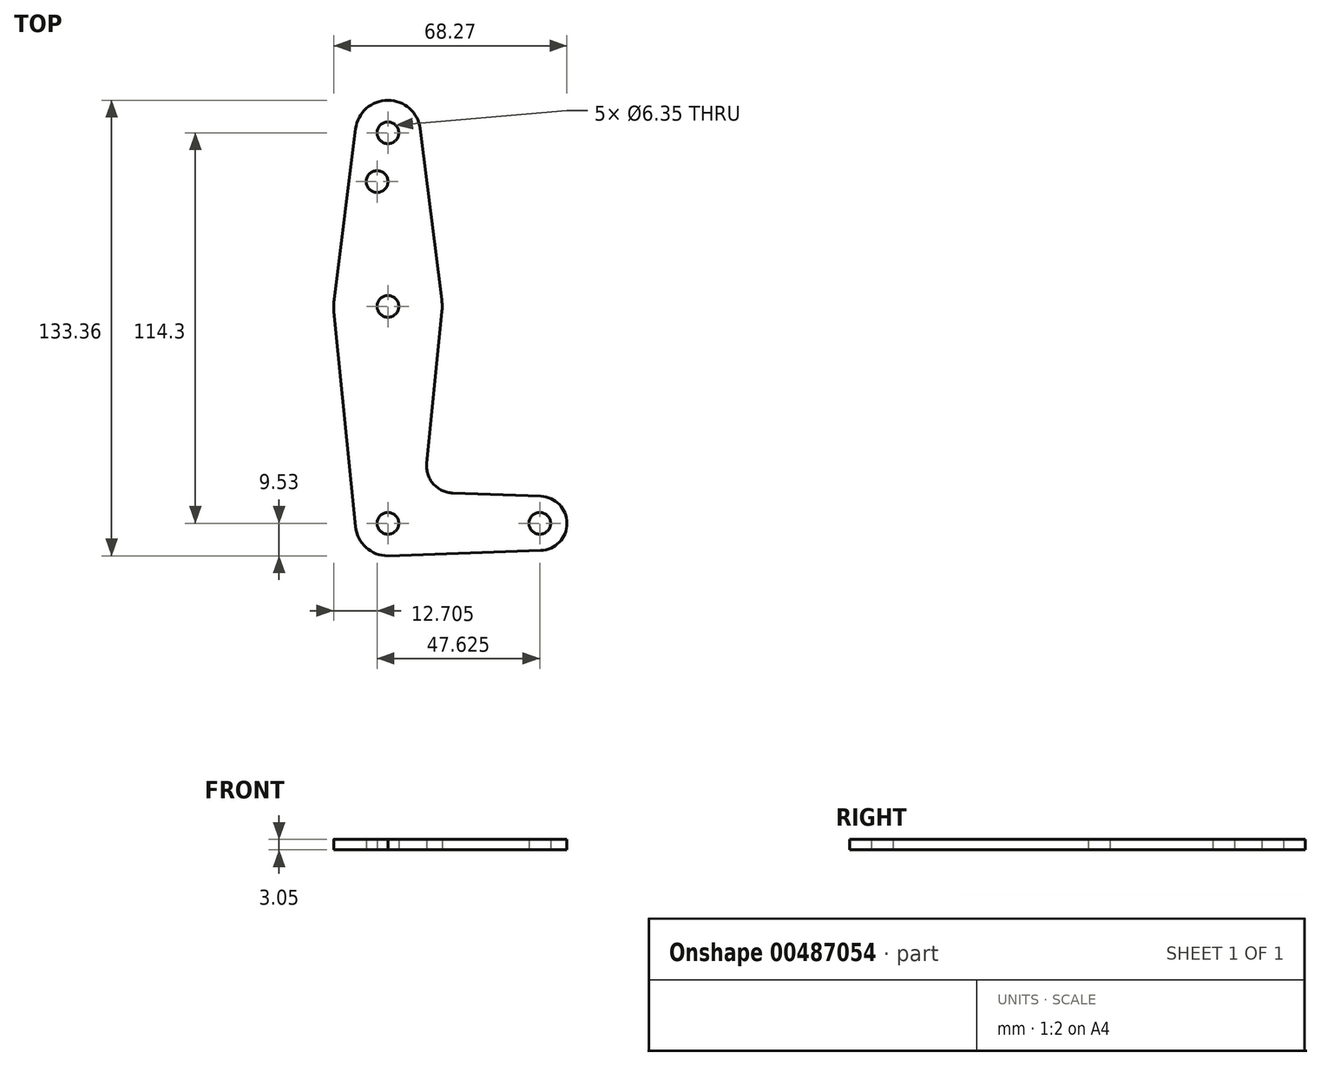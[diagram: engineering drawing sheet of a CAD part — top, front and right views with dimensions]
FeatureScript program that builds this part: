
annotation { "Feature Type Name" : "Feature", "Feature Type Description" : "" }
export const myFeature = defineFeature(function(context is Context, id is Id, definition is map)
    precondition{}
    {
        {
            var Q0;
            Q0=qCreatedBy(makeId("Top.planeOp"),FACE);
            var sketch = newSketch(context, id + "F0", { "sketchPlane" : qUnion([Q0])});
            skLineSegment(sketch, "E0", {"start": v(0, 0) * mm, "end": v(0, 114.3) * mm, "construction": true});
            skLineSegment(sketch, "E1", {"start": v(0, 0) * mm, "end": v(44.45, 0) * mm, "construction": true});
            skCircle(sketch, "E2", {"center": v(0, 0) * mm, "radius": 9.53 * mm});
            skCircle(sketch, "E3", {"center": v(44.45, 0) * mm, "radius": 7.94 * mm});
            skCircle(sketch, "E4", {"center": v(0, 114.3) * mm, "radius": 9.53 * mm});
            skCircle(sketch, "E5", {"center": v(0, 63.5) * mm, "radius": 15.88 * mm});
            skLineSegment(sketch, "E6", {"start": v(9.45, 115.5) * mm, "end": v(15.75, 65.48) * mm});
            skLineSegment(sketch, "E7", {"start": v(-9.45, 115.5) * mm, "end": v(-15.75, 65.48) * mm});
            skLineSegment(sketch, "E8", {"start": v(15.8, 61.91) * mm, "end": v(11.34, 17.59) * mm});
            skLineSegment(sketch, "E9", {"start": v(-15.8, 61.91) * mm, "end": v(-9.48, -0.95) * mm});
            skLineSegment(sketch, "E10", {"start": v(18.97, 8.85) * mm, "end": v(44.73, 7.93) * mm});
            skLineSegment(sketch, "E11", {"start": v(0, -9.53) * mm, "end": v(44.73, -7.93) * mm});
            skCircle(sketch, "E12", {"center": v(0, 114.3) * mm, "radius": 3.18 * mm});
            skCircle(sketch, "E13", {"center": v(-3.18, 100.03) * mm, "radius": 3.18 * mm});
            skCircle(sketch, "E14", {"center": v(0, 63.5) * mm, "radius": 3.18 * mm});
            skCircle(sketch, "E15", {"center": v(0, 0) * mm, "radius": 3.18 * mm});
            skCircle(sketch, "E16", {"center": v(44.45, 0) * mm, "radius": 3.18 * mm});
            skArc(sketch, "E17.filletArc", {"start": v(11.34, 17.59) * mm, "mid": v(13.26, 11.57) * mm, "end": v(18.97, 8.85) * mm});
            skSolve(sketch);
        }
        {
            var Q0;
            {var subQ1=sQuery(id+"F0.wireOp",EDGE,"E6");Q0=makeQuery(id+"F0.imprint","IMPRINT",FACE,{"disambiguationData":[TD([[makeQuery(id+"F0.imprint","IMPRINT",EDGE,{"derivedFrom":subQ1}),-1.0]])]});}
            var Q1;
            Q1=makeQuery(id+"F0.imprint","IMPRINT",FACE,{"disambiguationData":[TD([[makeQuery(id+"F0.imprint","IMPRINT",EDGE,{"derivedFrom":sQuery(id+"F0.wireOp",EDGE,"E12")}),-1.0]])]});
            var Q2;
            Q2=makeQuery(id+"F0.imprint","IMPRINT",FACE,{"disambiguationData":[TD([[makeQuery(id+"F0.imprint","IMPRINT",EDGE,{"derivedFrom":sQuery(id+"F0.wireOp",EDGE,"E14")}),-1.0]])]});
            var Q3;
            {var subQ0=sQuery(id+"F0.wireOp",EDGE,"E8");Q3=makeQuery(id+"F0.imprint","IMPRINT",FACE,{"disambiguationData":[TD([[makeQuery(id+"F0.imprint","IMPRINT",EDGE,{"derivedFrom":subQ0}),-1.0]])]});}
            var Q4;
            Q4=makeQuery(id+"F0.imprint","IMPRINT",FACE,{"disambiguationData":[TD([[makeQuery(id+"F0.imprint","IMPRINT",EDGE,{"derivedFrom":sQuery(id+"F0.wireOp",EDGE,"E15")}),-1.0]])]});
            var Q5;
            Q5=makeQuery(id+"F0.imprint","IMPRINT",FACE,{"disambiguationData":[TD([[makeQuery(id+"F0.imprint","IMPRINT",EDGE,{"derivedFrom":sQuery(id+"F0.wireOp",EDGE,"E16")}),-1.0]])]});
            extrude(context, id + "F1", {"entities" : qUnion([Q0, Q1, Q2, Q3, Q4, Q5]), "depth" : 3.05 * mm});
        }
    });
